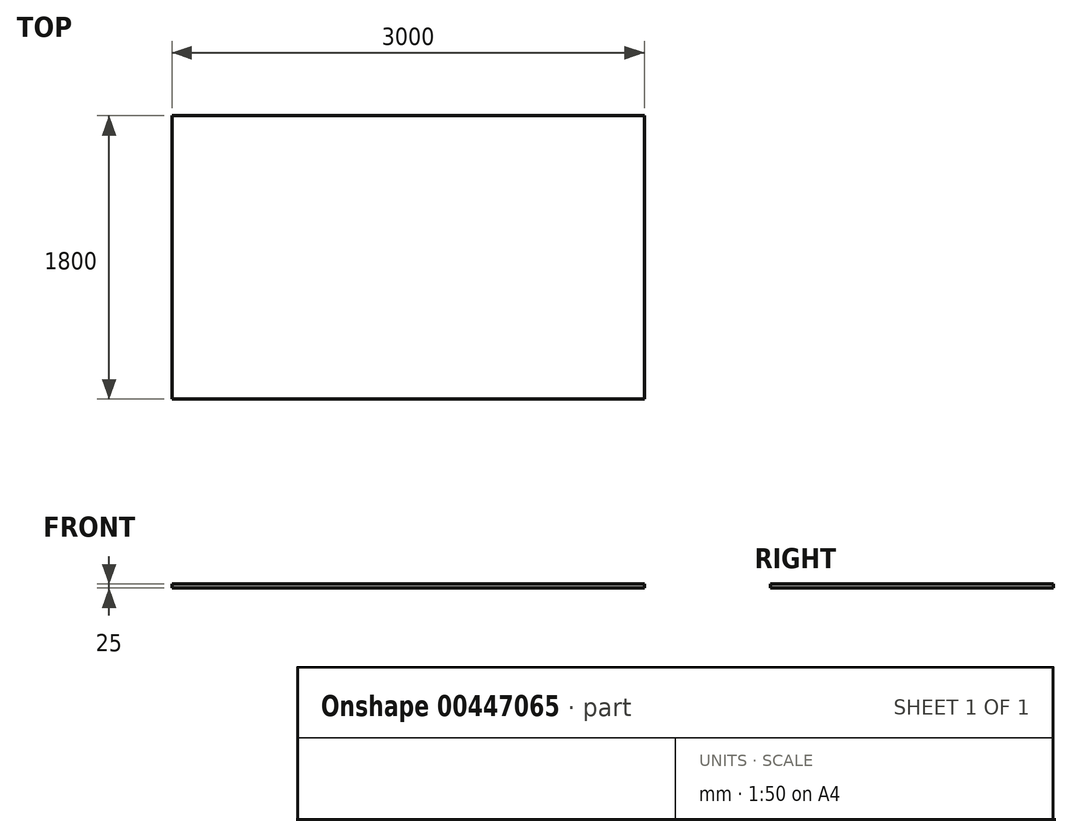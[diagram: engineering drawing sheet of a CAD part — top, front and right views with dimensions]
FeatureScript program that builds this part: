
annotation { "Feature Type Name" : "Feature", "Feature Type Description" : "" }
export const myFeature = defineFeature(function(context is Context, id is Id, definition is map)
    precondition{}
    {
        {
            var Q0;
            Q0=qCreatedBy(makeId("Top.planeOp"),FACE);
            var sketch = newSketch(context, id + "F0", { "sketchPlane" : qUnion([Q0])});
            skLineSegment(sketch, "E0.bottom", {"start": v(1500, -900) * mm, "end": v(-1500, -900) * mm});
            skLineSegment(sketch, "E0.top", {"start": v(1500, 900) * mm, "end": v(-1500, 900) * mm});
            skLineSegment(sketch, "E0.left", {"start": v(1500, -900) * mm, "end": v(1500, 900) * mm});
            skLineSegment(sketch, "E0.right", {"start": v(-1500, -900) * mm, "end": v(-1500, 900) * mm});
            skPoint(sketch, "E0.middle", {"position": v(0, 0) * mm});
            skSolve(sketch);
        }
        {
            var Q0;
            Q0=makeQuery(id+"F0.imprint","IMPRINT",FACE,{"disambiguationData":[TD([[makeQuery(id+"F0.imprint","IMPRINT",EDGE,{"derivedFrom":sQuery(id+"F0.wireOp",EDGE,"E0.bottom")}),-1.0]])]});
            extrude(context, id + "F1", {"entities" : qUnion([Q0]), "depth" : 25 * mm, "offsetDistance" : 25 * mm});
        }
    });
